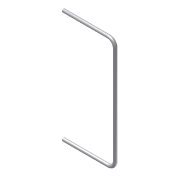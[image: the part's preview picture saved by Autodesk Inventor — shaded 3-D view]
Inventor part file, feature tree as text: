
AUTODESK INVENTOR PART (.ipt)
format: ipt  version: 2012 (Build 160160000, 160)  size: 88,064 bytes
history: native  units: in
note: dims shown in document units (in); Inventor stores cm internally (conversion verified against a paired STEP export)
features: sketch x2, plane x1, sweep x1, shell x1
ambient origin geometry x8: Origin, YZ Plane, XZ Plane, XY Plane, X Axis, Y Axis, Z Axis, Center Point
bodies: Solid1 (feature_tree)
feature tree (5):
  sketch  "Sketch1"  dims[d2=2.6575in d3=2.6575in d4=44.6875in]
  plane  "Work Plane1"
  sweep  "Sweep1"
  shell  "Shell1"  Thickness=44.6875in
  sketch  "Sketch2"  dims[d5=20.6575in d6=1.315in d7=0.0in d8=0.133in]
